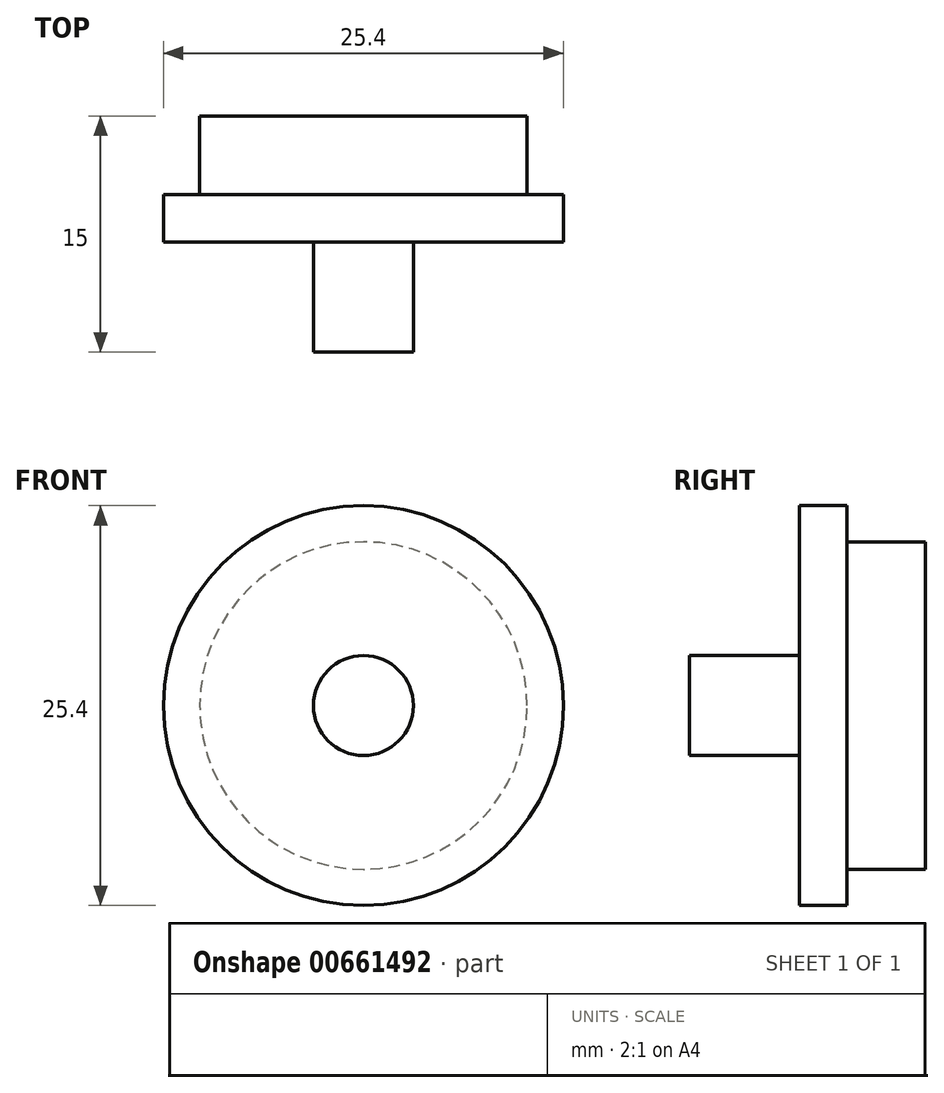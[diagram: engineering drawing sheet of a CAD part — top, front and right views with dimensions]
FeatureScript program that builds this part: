
annotation { "Feature Type Name" : "Feature", "Feature Type Description" : "" }
export const myFeature = defineFeature(function(context is Context, id is Id, definition is map)
    precondition{}
    {
        {
            var Q0;
            Q0=qCreatedBy(makeId("Front.planeOp"),FACE);
            var sketch = newSketch(context, id + "F0", { "sketchPlane" : qUnion([Q0])});
            skCircle(sketch, "E0", {"center": v(0, 0) * mm, "radius": 10.4 * mm});
            skCircle(sketch, "E1", {"center": v(0, 0) * mm, "radius": 12.7 * mm});
            skSolve(sketch);
        }
        {
            var Q0;
            Q0=makeQuery(id+"F0.imprint","IMPRINT",FACE,{"disambiguationData":[TD([[makeQuery(id+"F0.imprint","IMPRINT",EDGE,{"derivedFrom":sQuery(id+"F0.wireOp",EDGE,"E0")}),1.0]])]});
            extrude(context, id + "F1", {"entities" : qUnion([Q0]), "oppositeDirection" : true, "depth" : 5 * mm, "offsetDistance" : 25 * mm});
        }
        {
            var Q0;
            Q0=makeQuery(id+"F0.imprint","IMPRINT",FACE,{"disambiguationData":[TD([[makeQuery(id+"F0.imprint","IMPRINT",EDGE,{"derivedFrom":sQuery(id+"F0.wireOp",EDGE,"E0")}),-1.0]])]});
            var Q1;
            Q1=makeQuery(id+"F0.imprint","IMPRINT",FACE,{"disambiguationData":[TD([[makeQuery(id+"F0.imprint","IMPRINT",EDGE,{"derivedFrom":sQuery(id+"F0.wireOp",EDGE,"E0")}),1.0]])]});
            extrude(context, id + "F2", {"entities" : qUnion([Q0, Q1]), "operationType" : NewBodyOperationType.ADD, "depth" : 3 * mm, "offsetDistance" : 25 * mm});
        }
        {
            var Q0;
            Q0=makeQuery(id+"F2.opExtrude","CAP_FACE",FACE,{"disambiguationData":[OSD([sQuery(id+"F0.wireOp",EDGE,"E1")])],"isStart":false});
            var sketch = newSketch(context, id + "F3", { "sketchPlane" : qUnion([Q0])});
            skCircle(sketch, "E2", {"center": v(0, 0) * mm, "radius": 3.17 * mm});
            skSolve(sketch);
        }
        {
            var Q0;
            Q0=makeQuery(id+"F3.imprint","IMPRINT",FACE,{"disambiguationData":[TD([[makeQuery(id+"F3.imprint","IMPRINT",EDGE,{"derivedFrom":sQuery(id+"F3.wireOp",EDGE,"E2")}),1.0]])]});
            extrude(context, id + "F4", {"entities" : qUnion([Q0]), "operationType" : NewBodyOperationType.ADD, "depth" : 7 * mm, "offsetDistance" : 25 * mm});
        }
    });
